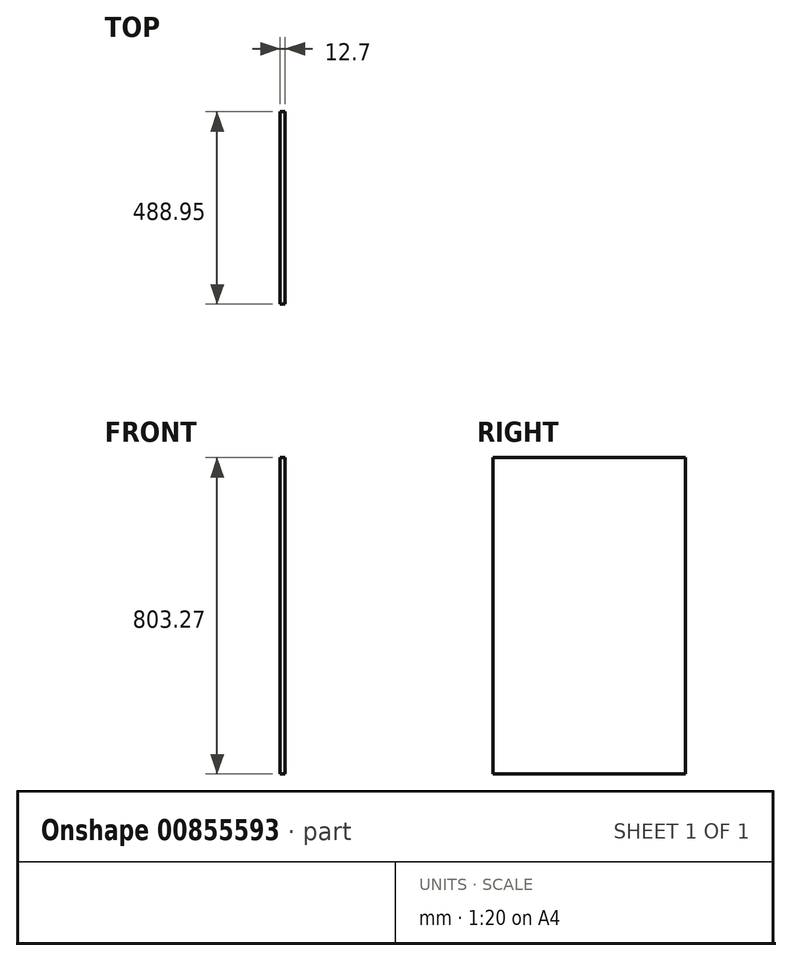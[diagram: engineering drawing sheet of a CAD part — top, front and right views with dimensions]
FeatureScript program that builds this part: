
annotation { "Feature Type Name" : "Feature", "Feature Type Description" : "" }
export const myFeature = defineFeature(function(context is Context, id is Id, definition is map)
    precondition{}
    {
        {
            var Q0;
            Q0=qCreatedBy(makeId("Right.planeOp"),FACE);
            var sketch = newSketch(context, id + "F0", { "sketchPlane" : qUnion([Q0])});
            skLineSegment(sketch, "E0.bottom", {"start": v(0, 0) * mm, "end": v(488.95, 0) * mm});
            skLineSegment(sketch, "E0.top", {"start": v(0, 803.28) * mm, "end": v(488.95, 803.28) * mm});
            skLineSegment(sketch, "E0.left", {"start": v(0, 0) * mm, "end": v(0, 803.28) * mm});
            skLineSegment(sketch, "E0.right", {"start": v(488.95, 0) * mm, "end": v(488.95, 803.28) * mm});
            skSolve(sketch);
        }
        {
            var Q0;
            Q0=qSketchRegion(id+"F0",true);
            extrude(context, id + "F1", {"entities" : qUnion([Q0]), "depth" : 12.7 * mm, "offsetDistance" : 25.4 * mm});
        }
    });
